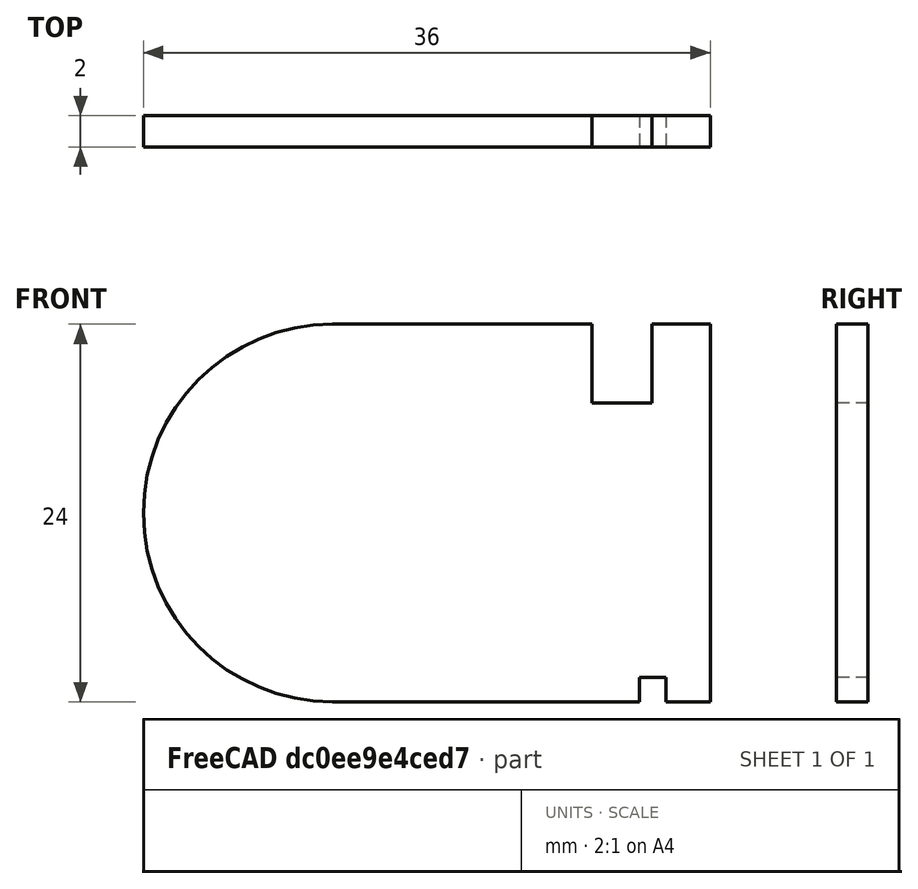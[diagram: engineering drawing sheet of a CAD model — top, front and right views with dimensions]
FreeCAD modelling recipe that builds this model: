
FCSTD DOCUMENT  (FreeCAD 1.0R)
Label: CW-Pad-Basic
License: All rights reserved
LicenseURL: https://en.wikipedia.org/wiki/All_rights_reserved
objects: Sketcher::SketchObject×1, PartDesign::Pad×1, PartDesign::Body×1, Part::Part2DObjectPython×1
note: 7 computed .brp shape members not serialized (recipe doc carries the construction recipe); baked Part::Feature solids carry a one-line shape summary decoded from their .brp

FEATURE [Sketcher::SketchObject] Sketch
  ArcFitTolerance = 1e-06
  AttachmentSupport = -> [XZ_Plane]
  FullyConstrained = true
  MakeInternals = false
  MapMode = 5
  Placement = pos=(0,0,0) rot=(1,0,0;1.5708rad)
  sketch-geometry (19):
    g0: GeomPoint [constr] X=0 Y=0 Z=0
    g1: GeomPoint [constr] X=0 Y=0 Z=0
    g2: LineSegment StartX=-15 StartY=-12 StartZ=0 EndX=4.5 EndY=-12 EndZ=0
    g3: LineSegment StartX=9 StartY=-12 StartZ=0 EndX=9 EndY=12 EndZ=0
    g4: LineSegment StartX=9 StartY=12 StartZ=0 EndX=5.3 EndY=12 EndZ=0
    g5: GeomPoint [constr] X=-3 Y=0 Z=0
    g6: ArcOfCircle CenterX=-15 CenterY=3e-16 CenterZ=0 NormalX=0 NormalY=0 NormalZ=1 AngleXU=0 Radius=12 StartAngle=1.5708 EndAngle=4.71239
    g7: LineSegment StartX=6.2 StartY=-12 StartZ=0 EndX=6.2 EndY=-10.45 EndZ=0
    g8: LineSegment StartX=6.2 StartY=-10.45 StartZ=0 EndX=4.5 EndY=-10.45 EndZ=0
    g9: LineSegment StartX=4.5 StartY=-10.45 StartZ=0 EndX=4.5 EndY=-12 EndZ=0
    g10: GeomPoint [constr] X=5.35 Y=-11.225 Z=0
    g11: LineSegment StartX=6.2 StartY=-12 StartZ=0 EndX=9 EndY=-12 EndZ=0
    g12: LineSegment StartX=1.5 StartY=7 StartZ=0 EndX=5.3 EndY=7 EndZ=0
    g13: LineSegment StartX=5.3 StartY=7 StartZ=0 EndX=5.3 EndY=12 EndZ=0
    g14: LineSegment StartX=1.5 StartY=12 StartZ=0 EndX=1.5 EndY=7 EndZ=0
    g15: GeomPoint [constr] X=3.4 Y=9.5 Z=0
    g16: LineSegment StartX=1.5 StartY=12 StartZ=0 EndX=-15 EndY=12 EndZ=0
    g17: Circle [constr] CenterX=-15 CenterY=3e-16 CenterZ=0 NormalX=0 NormalY=0 NormalZ=1 AngleXU=0 Radius=9.875
    g18: LineSegment [constr] StartX=1.5 StartY=30 StartZ=0 EndX=1.5 EndY=-30 EndZ=0
  constraints (46):
    c: Coincident(g0,g-1)
    c: Coincident(g1,g0)
    c: Coincident(g11,g3)
    c: Coincident(g3,g4)
    c: Horizontal(g2)
    c: Horizontal(g4)
    c: Vertical(g3)
    c: Symmetric(g4,g2,g5)
    c: Distance(g2,g16) = 24
    c: Horizontal(g5,g0)
    c: Coincident(g6,g2)
    c: Coincident(g6,g16)
    c: DistanceX(g6,g0) = 15
    c: Coincident(g7,g8)
    c: Coincident(g8,g9)
    c: Horizontal(g8)
    c: Vertical(g7)
    c: Vertical(g9)
    c: Symmetric(g8,g9,g10)
    c: DistanceX(g0,g9) = 4.5
    c: Equal(g9,g7)
    c: Parallel(g11,g2)
    c: Coincident(g7,g11)
    c: Coincident(g9,g2)
    c: Coincident(g12,g13)
    c: Coincident(g14,g12)
    c: Horizontal(g12)
    c: Vertical(g13)
    c: Vertical(g14)
    c: Symmetric(g13,g12,g15)
    c: DistanceX(g0,g14) = 1.5
    c: Coincident(g16,g14)
    c: Parallel(g16,g2)
    c: DistanceX(g14,g4) = 3.8
    c: Diameter(g17) = 19.75
    c: Coincident(g17,g6)
    c: DistanceY(g18,g18) = 60
    c: DistanceX(g0,g18) = 1.5
    c: Symmetric(g18,g18,g-1)
    c: DistanceY(g2,g8) = 1.55
    c: DistanceX(g2,g7) = 1.7
    c: Symmetric(g6,g2,g-1)
    c: DistanceX(g0,g3) = 9
    c: Coincident(g13,g4)
    c: DistanceY(g12,g4) = 5
    c: Vertical(g6,g6)
FEATURE [PartDesign::Pad] Pad
  Direction = (0,-1,2e-16)
  Length = 2
  Length2 = 10
  Midplane = true
  Placement = pos=(0,0,0) rot=(1,0,0;1.5708rad)
  Profile = -> Sketch
  ReferenceAxis = -> Sketch [N_Axis]
  Refine = true
  Suppressed = false
  Type = 0
FEATURE [PartDesign::Body] Body  label="CW-Pad-Base"
  AllowCompound = false
  Group = -> [Sketch,Pad]
  Origin = -> Origin
  Tip = -> Pad
FEATURE [Part::Part2DObjectPython] Shape2DView  # Draft 2D object (typed FeaturePython)
  AutoUpdate = true
  Base = -> Pad
  Clip = false
  FuseArch = false
  HiddenLines = false
  InPlace = true
  OnlySolids = false
  Projection = (0,-1,0)
  ProjectionMode = 0
  SegmentLength = 0.05
  Tessellation = false
  VisibleOnly = false
